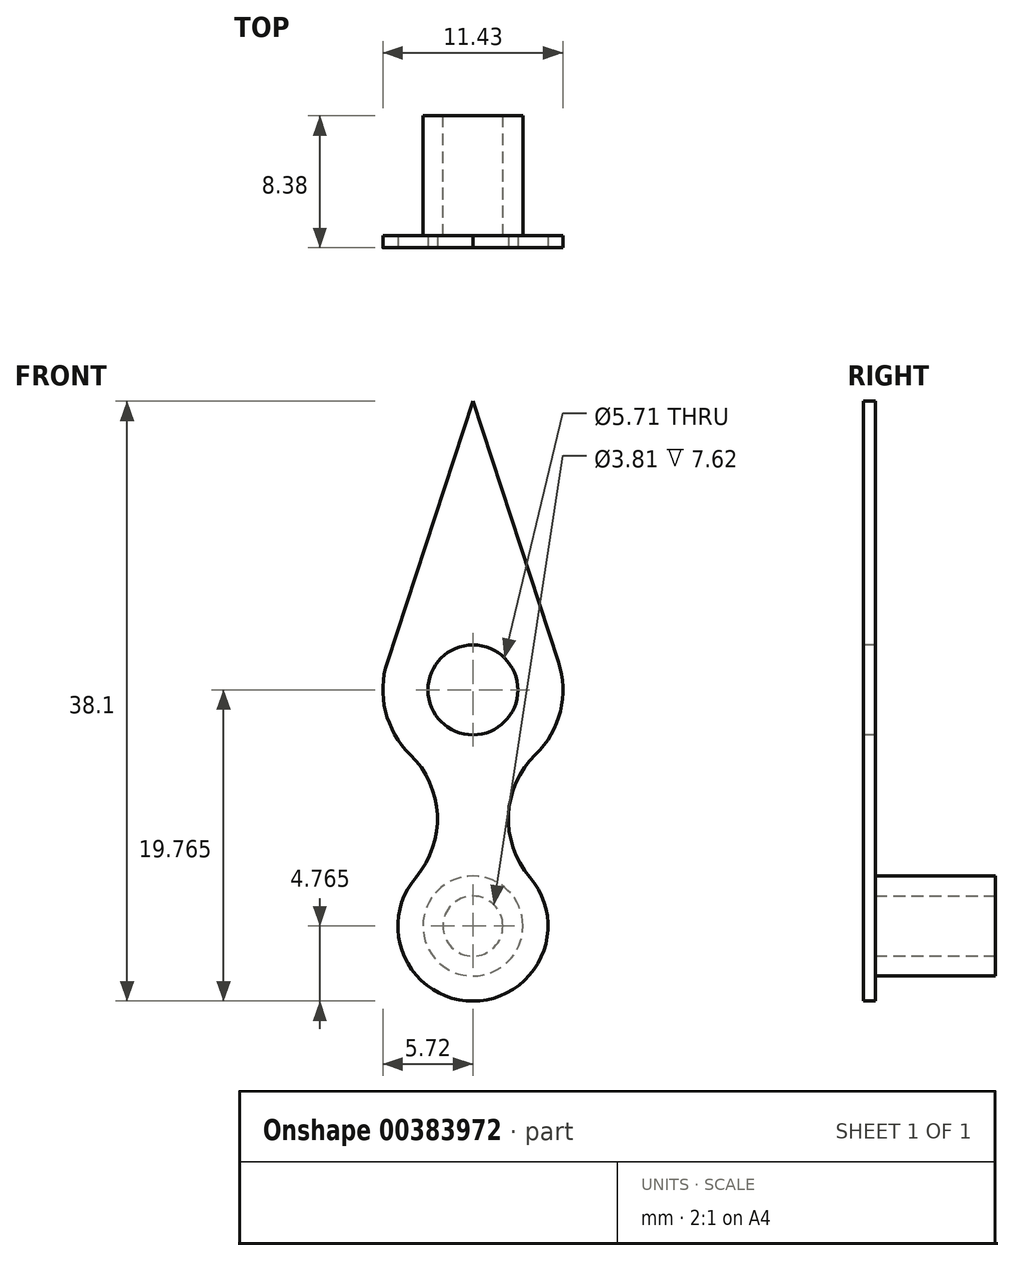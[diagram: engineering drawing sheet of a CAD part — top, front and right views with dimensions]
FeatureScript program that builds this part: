
annotation { "Feature Type Name" : "Feature", "Feature Type Description" : "" }
export const myFeature = defineFeature(function(context is Context, id is Id, definition is map)
    precondition{}
    {
        {
            var Q0;
            Q0=qCreatedBy(makeId("Front.planeOp"),FACE);
            var sketch = newSketch(context, id + "F0", { "sketchPlane" : qUnion([Q0])});
            skLineSegment(sketch, "E0", {"start": v(0, 0) * mm, "end": v(0, 38.1) * mm});
            skArc(sketch, "E1", {"start": v(-3.62, 7.86) * mm, "mid": v(0, 0) * mm, "end": v(3.62, 7.86) * mm});
            skArc(sketch, "E2", {"start": v(-5.43, 21.55) * mm, "mid": v(-5.55, 18.4) * mm, "end": v(-3.98, 15.67) * mm});
            skCircle(sketch, "E3", {"center": v(0, 19.76) * mm, "radius": 2.86 * mm});
            skLineSegment(sketch, "E4", {"start": v(0, 38.1) * mm, "end": v(-5.43, 21.55) * mm});
            skLineSegment(sketch, "E5", {"start": v(0, 38.1) * mm, "end": v(5.43, 21.55) * mm});
            skArc(sketch, "E6", {"start": v(-3.62, 7.86) * mm, "mid": v(-2.26, 11.84) * mm, "end": v(-3.98, 15.67) * mm});
            skArc(sketch, "E7", {"start": v(3.98, 15.67) * mm, "mid": v(2.26, 11.84) * mm, "end": v(3.62, 7.86) * mm});
            skArc(sketch, "E8.trimOffspring", {"start": v(3.98, 15.67) * mm, "mid": v(5.55, 18.4) * mm, "end": v(5.43, 21.55) * mm});
            skSolve(sketch);
        }
        {
            var Q0;
            {var subQ7=sQuery(id+"F0.wireOp",EDGE,"E5");Q0=makeQuery(id+"F0.imprint","IMPRINT",FACE,{"disambiguationData":[TD([[makeQuery(id+"F0.imprint","IMPRINT",EDGE,{"derivedFrom":subQ7}),-1.0]])]});}
            var Q1;
            Q1=makeQuery(id+"F0.imprint","IMPRINT",FACE,{"disambiguationData":[TD([[makeQuery(id+"F0.imprint","IMPRINT",EDGE,{"derivedFrom":sQuery(id+"F0.wireOp",EDGE,"E2")}),1.0]])]});
            extrude(context, id + "F1", {"entities" : qUnion([Q0, Q1]), "endBound" : BoundingType.SYMMETRIC, "oppositeDirection" : true, "depth" : 0.76 * mm});
        }
        {
            var Q0;
            Q0=makeQuery(id+"F1.opExtrude","CAP_FACE",FACE,{"disambiguationData":[OSD([sQuery(id+"F0.wireOp",EDGE,"E1"),sQuery(id+"F0.wireOp",EDGE,"E2"),sQuery(id+"F0.wireOp",EDGE,"E3"),sQuery(id+"F0.wireOp",EDGE,"E4"),sQuery(id+"F0.wireOp",EDGE,"E5"),sQuery(id+"F0.wireOp",EDGE,"E6"),sQuery(id+"F0.wireOp",EDGE,"E7"),sQuery(id+"F0.wireOp",EDGE,"E8.trimOffspring")])],"isStart":false});
            var sketch = newSketch(context, id + "F2", { "sketchPlane" : qUnion([Q0])});
            skCircle(sketch, "E9", {"center": v(0, 4.77) * mm, "radius": 3.18 * mm});
            skSolve(sketch);
        }
        {
            var Q0;
            Q0=makeQuery(id+"F2.imprint","IMPRINT",FACE,{"disambiguationData":[TD([[makeQuery(id+"F2.imprint","IMPRINT",EDGE,{"derivedFrom":sQuery(id+"F2.wireOp",EDGE,"E9")}),1.0]])]});
            extrude(context, id + "F3", {"entities" : qUnion([Q0]), "operationType" : NewBodyOperationType.ADD, "depth" : 7.62 * mm});
        }
        {
            var Q0;
            Q0=makeQuery(id+"F3.opExtrude","CAP_FACE",FACE,{"disambiguationData":[OSD([sQuery(id+"F2.wireOp",EDGE,"E9")])],"isStart":false});
            var sketch = newSketch(context, id + "F4", { "sketchPlane" : qUnion([Q0])});
            skCircle(sketch, "E10", {"center": v(0, 4.77) * mm, "radius": 1.9 * mm});
            skSolve(sketch);
        }
        {
            var Q0;
            Q0=makeQuery(id+"F4.imprint","IMPRINT",FACE,{"disambiguationData":[TD([[makeQuery(id+"F4.imprint","IMPRINT",EDGE,{"derivedFrom":sQuery(id+"F4.wireOp",EDGE,"E10")}),1.0]])]});
            extrude(context, id + "F5", {"entities" : qUnion([Q0]), "operationType" : NewBodyOperationType.REMOVE, "oppositeDirection" : true, "depth" : 7.62 * mm});
        }
    });
